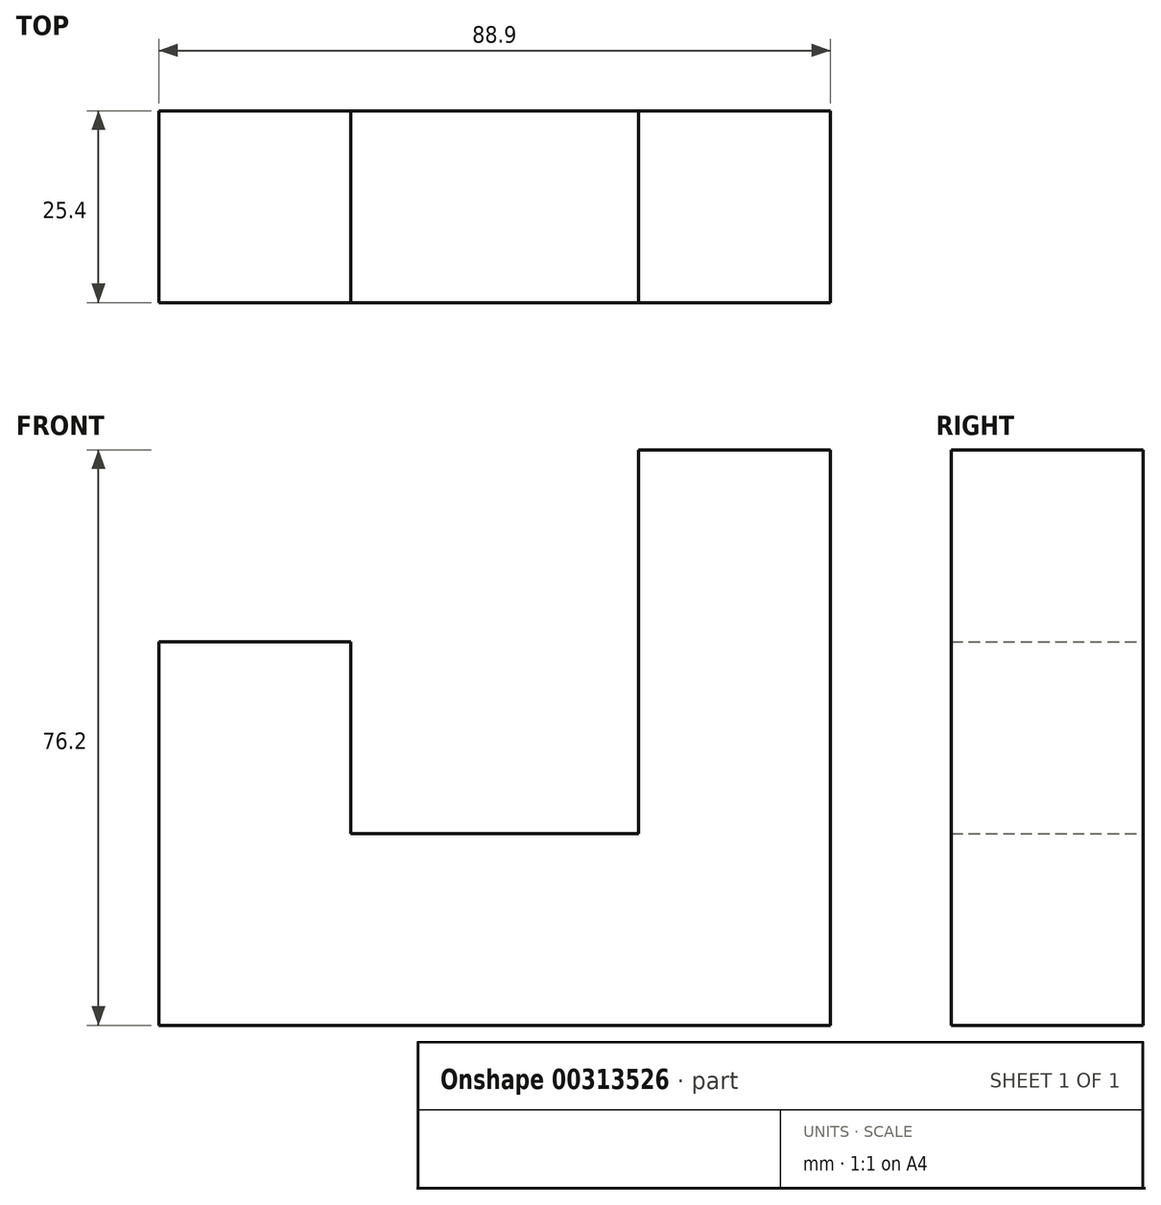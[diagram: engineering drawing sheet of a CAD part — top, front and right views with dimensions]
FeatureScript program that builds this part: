
annotation { "Feature Type Name" : "Feature", "Feature Type Description" : "" }
export const myFeature = defineFeature(function(context is Context, id is Id, definition is map)
    precondition{}
    {
        {
            var Q0;
            Q0=qCreatedBy(makeId("Front.planeOp"),FACE);
            var sketch = newSketch(context, id + "F0", { "sketchPlane" : qUnion([Q0])});
            skLineSegment(sketch, "E0", {"start": v(-37.18, -45.22) * mm, "end": v(51.72, -45.22) * mm});
            skLineSegment(sketch, "E1", {"start": v(51.72, -45.22) * mm, "end": v(51.72, 30.98) * mm});
            skLineSegment(sketch, "E2", {"start": v(51.72, 30.98) * mm, "end": v(26.32, 30.98) * mm});
            skLineSegment(sketch, "E3", {"start": v(26.32, 30.98) * mm, "end": v(26.32, -19.82) * mm});
            skLineSegment(sketch, "E4", {"start": v(26.32, -19.82) * mm, "end": v(-11.78, -19.82) * mm});
            skLineSegment(sketch, "E5", {"start": v(-11.78, -19.82) * mm, "end": v(-11.78, 5.58) * mm});
            skLineSegment(sketch, "E6", {"start": v(-11.78, 5.58) * mm, "end": v(-37.18, 5.58) * mm});
            skLineSegment(sketch, "E7", {"start": v(-37.18, 5.58) * mm, "end": v(-37.18, -45.22) * mm});
            skSolve(sketch);
        }
        {
            var Q0;
            Q0=makeQuery(id+"F0.imprint","IMPRINT",FACE,{"disambiguationData":[TD([[makeQuery(id+"F0.imprint","IMPRINT",EDGE,{"derivedFrom":sQuery(id+"F0.wireOp",EDGE,"E0")}),1.0]])]});
            extrude(context, id + "F1", {"entities" : qUnion([Q0]), "depth" : 25.4 * mm});
        }
    });
